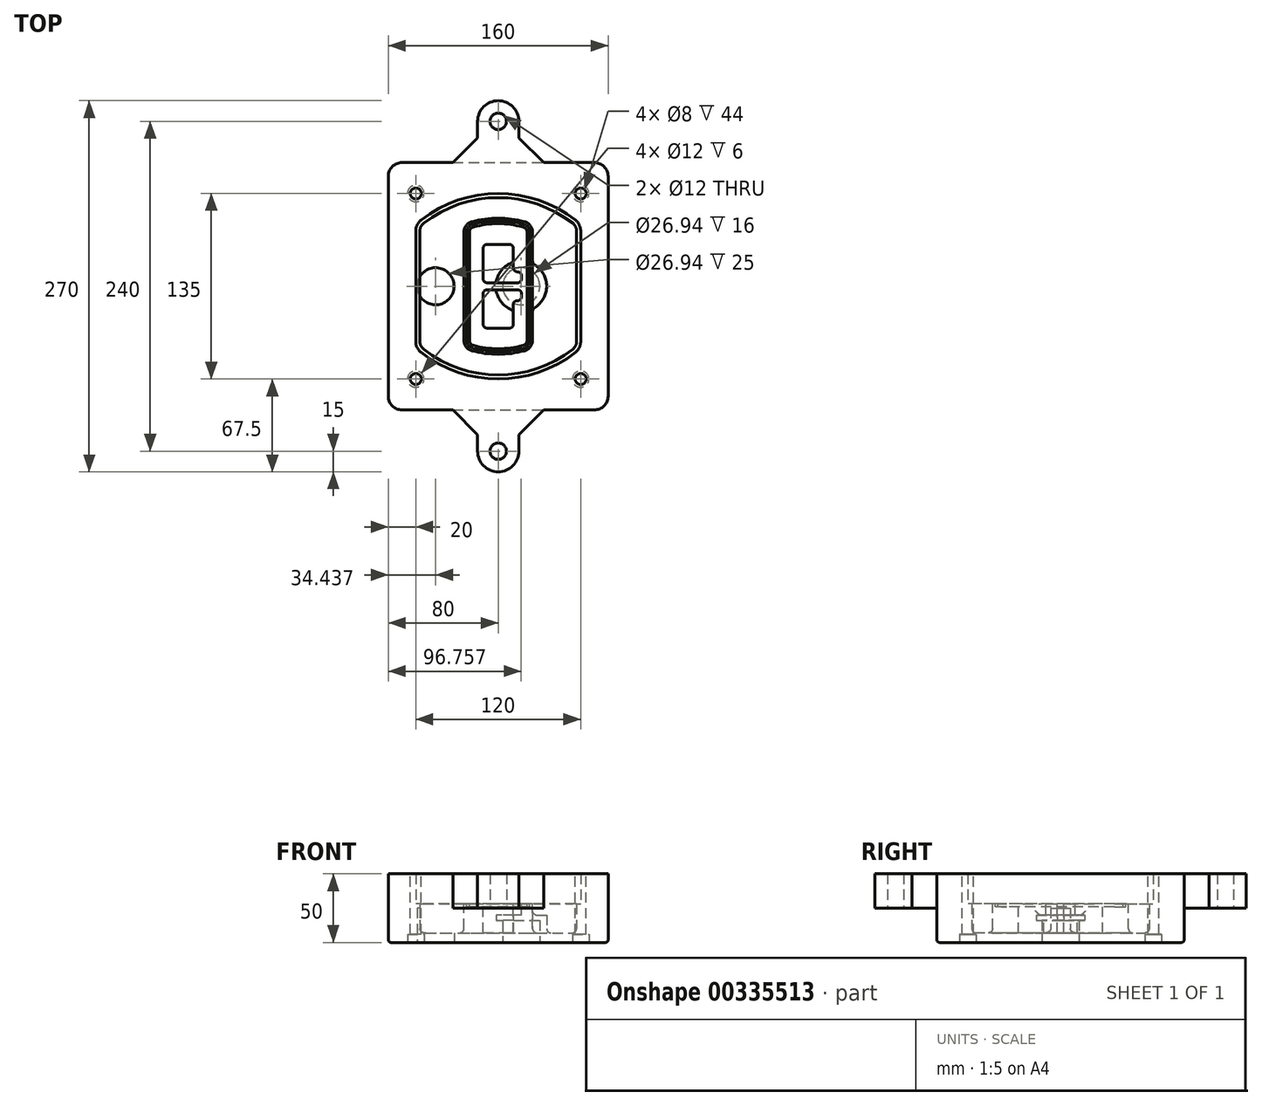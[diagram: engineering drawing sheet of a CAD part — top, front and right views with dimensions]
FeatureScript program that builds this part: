
annotation { "Feature Type Name" : "Feature", "Feature Type Description" : "" }
export const myFeature = defineFeature(function(context is Context, id is Id, definition is map)
    precondition{}
    {
        {
            var Q0;
            Q0=qCreatedBy(makeId("Top.planeOp"),FACE);
            var sketch = newSketch(context, id + "F0", { "sketchPlane" : qUnion([Q0])});
            skPoint(sketch, "E0.rect.middle", {"position": v(0, 0) * mm});
            skLineSegment(sketch, "E1.bottom", {"start": v(-70, -90) * mm, "end": v(70, -90) * mm});
            skLineSegment(sketch, "E1.top", {"start": v(-70, 90) * mm, "end": v(70, 90) * mm});
            skLineSegment(sketch, "E1.left", {"start": v(-80, -80) * mm, "end": v(-80, 80) * mm});
            skLineSegment(sketch, "E1.right", {"start": v(80, -80) * mm, "end": v(80, 80) * mm});
            skLineSegment(sketch, "E2", {"start": v(-80, 90) * mm, "end": v(80, -90) * mm, "construction": true});
            skLineSegment(sketch, "E3", {"start": v(80, 90) * mm, "end": v(-80, -90) * mm, "construction": true});
            skCircle(sketch, "E4", {"center": v(-60, 67.5) * mm, "radius": 4 * mm});
            skCircle(sketch, "E5", {"center": v(60, 67.5) * mm, "radius": 4 * mm});
            skCircle(sketch, "E6", {"center": v(60, -67.5) * mm, "radius": 4 * mm});
            skCircle(sketch, "E7", {"center": v(-60, -67.5) * mm, "radius": 4 * mm});
            skLineSegment(sketch, "E8", {"start": v(-60, 67.5) * mm, "end": v(60, 67.5) * mm, "construction": true});
            skLineSegment(sketch, "E9", {"start": v(60, 67.5) * mm, "end": v(60, -67.5) * mm, "construction": true});
            skLineSegment(sketch, "E10", {"start": v(60, -67.5) * mm, "end": v(-60, -67.5) * mm, "construction": true});
            skLineSegment(sketch, "E11", {"start": v(-60, -67.5) * mm, "end": v(-60, 67.5) * mm, "construction": true});
            skLineSegment(sketch, "E12", {"start": v(-60, 40.3) * mm, "end": v(-60, -40.3) * mm});
            skLineSegment(sketch, "E13", {"start": v(60, 40.3) * mm, "end": v(60, -40.3) * mm});
            skArc(sketch, "E14", {"start": v(56.15, 48.18) * mm, "mid": v(0, 67.5) * mm, "end": v(-56.15, 48.18) * mm});
            skArc(sketch, "E15", {"start": v(-56.15, -48.18) * mm, "mid": v(0, -67.5) * mm, "end": v(56.15, -48.18) * mm});
            skLineSegment(sketch, "E16", {"start": v(-60, 0) * mm, "end": v(60, 0) * mm, "construction": true});
            skPoint(sketch, "E17.visualSharp", {"position": v(-60, -45) * mm});
            skArc(sketch, "E17.filletArc", {"start": v(-60, -40.3) * mm, "mid": v(-58.99, -44.68) * mm, "end": v(-56.15, -48.18) * mm});
            skPoint(sketch, "E18.visualSharp", {"position": v(-60, 45) * mm});
            skArc(sketch, "E18.filletArc", {"start": v(-56.15, 48.18) * mm, "mid": v(-58.99, 44.68) * mm, "end": v(-60, 40.3) * mm});
            skPoint(sketch, "E19.visualSharp", {"position": v(60, 45) * mm});
            skArc(sketch, "E19.filletArc", {"start": v(60, 40.3) * mm, "mid": v(58.99, 44.68) * mm, "end": v(56.15, 48.18) * mm});
            skPoint(sketch, "E20.visualSharp", {"position": v(60, -45) * mm});
            skArc(sketch, "E20.filletArc", {"start": v(56.15, -48.18) * mm, "mid": v(58.99, -44.68) * mm, "end": v(60, -40.3) * mm});
            skPoint(sketch, "E21.visualSharp", {"position": v(-80, 90) * mm});
            skArc(sketch, "E21.filletArc", {"start": v(-70, 90) * mm, "mid": v(-77.07, 87.07) * mm, "end": v(-80, 80) * mm});
            skPoint(sketch, "E22.visualSharp", {"position": v(80, 90) * mm});
            skArc(sketch, "E22.filletArc", {"start": v(80, 80) * mm, "mid": v(77.07, 87.07) * mm, "end": v(70, 90) * mm});
            skPoint(sketch, "E23.visualSharp", {"position": v(80, -90) * mm});
            skArc(sketch, "E23.filletArc", {"start": v(70, -90) * mm, "mid": v(77.07, -87.07) * mm, "end": v(80, -80) * mm});
            skPoint(sketch, "E24.visualSharp", {"position": v(-80, -90) * mm});
            skArc(sketch, "E24.filletArc", {"start": v(-80, -80) * mm, "mid": v(-77.07, -87.07) * mm, "end": v(-70, -90) * mm});
            skArc(sketch, "E25.0", {"start": v(57, 40.3) * mm, "mid": v(56.3, 43.36) * mm, "end": v(54.3, 45.81) * mm});
            skLineSegment(sketch, "E25.1", {"start": v(57, 40.3) * mm, "end": v(57, -40.3) * mm});
            skArc(sketch, "E25.2", {"start": v(54.3, -45.81) * mm, "mid": v(56.3, -43.36) * mm, "end": v(57, -40.3) * mm});
            skArc(sketch, "E25.3", {"start": v(-54.3, -45.81) * mm, "mid": v(0, -64.5) * mm, "end": v(54.3, -45.81) * mm});
            skArc(sketch, "E25.4", {"start": v(-57, -40.3) * mm, "mid": v(-56.3, -43.36) * mm, "end": v(-54.3, -45.81) * mm});
            skArc(sketch, "E25.5", {"start": v(54.3, 45.81) * mm, "mid": v(0, 64.5) * mm, "end": v(-54.3, 45.81) * mm});
            skLineSegment(sketch, "E25.6", {"start": v(-57, 40.3) * mm, "end": v(-57, -40.3) * mm});
            skArc(sketch, "E25.7", {"start": v(-54.3, 45.81) * mm, "mid": v(-56.3, 43.36) * mm, "end": v(-57, 40.3) * mm});
            skArc(sketch, "E26.0", {"start": v(-58.62, 51.33) * mm, "mid": v(-62.58, 46.43) * mm, "end": v(-64, 40.3) * mm});
            skArc(sketch, "E26.1", {"start": v(58.62, 51.33) * mm, "mid": v(0, 71.5) * mm, "end": v(-58.62, 51.33) * mm});
            skArc(sketch, "E26.2", {"start": v(64, 40.3) * mm, "mid": v(62.58, 46.43) * mm, "end": v(58.62, 51.33) * mm});
            skLineSegment(sketch, "E26.3", {"start": v(64, 40.3) * mm, "end": v(64, -40.3) * mm});
            skArc(sketch, "E26.4", {"start": v(58.62, -51.33) * mm, "mid": v(62.58, -46.43) * mm, "end": v(64, -40.3) * mm});
            skLineSegment(sketch, "E26.5", {"start": v(-64, 40.3) * mm, "end": v(-64, -40.3) * mm});
            skArc(sketch, "E26.6", {"start": v(-58.62, -51.33) * mm, "mid": v(0, -71.5) * mm, "end": v(58.62, -51.33) * mm});
            skArc(sketch, "E26.7", {"start": v(-64, -40.3) * mm, "mid": v(-62.58, -46.43) * mm, "end": v(-58.62, -51.33) * mm});
            skSolve(sketch);
        }
        {
            var Q0;
            Q0=makeQuery(id+"F0.imprint","IMPRINT",FACE,{"disambiguationData":[TD([[makeQuery(id+"F0.imprint","IMPRINT",EDGE,{"derivedFrom":sQuery(id+"F0.wireOp",EDGE,"E1.bottom")}),1.0]])]});
            var Q1;
            Q1=makeQuery(id+"F0.imprint","IMPRINT",FACE,{"disambiguationData":[TD([[makeQuery(id+"F0.imprint","IMPRINT",EDGE,{"derivedFrom":sQuery(id+"F0.wireOp",EDGE,"E12")}),1.0]])]});
            var Q2;
            Q2=makeQuery(id+"F0.imprint","IMPRINT",FACE,{"disambiguationData":[TD([[makeQuery(id+"F0.imprint","IMPRINT",EDGE,{"derivedFrom":sQuery(id+"F0.wireOp",EDGE,"E25.0")}),1.0]])]});
            var Q3;
            Q3=makeQuery(id+"F0.imprint","IMPRINT",FACE,{"disambiguationData":[TD([[makeQuery(id+"F0.imprint","IMPRINT",EDGE,{"derivedFrom":sQuery(id+"F0.wireOp",EDGE,"E12")}),-1.0]])]});
            extrude(context, id + "F1", {"entities" : qUnion([Q0, Q1, Q2, Q3]), "oppositeDirection" : true, "depth" : 25 * mm});
        }
        {
            var Q0;
            Q0=makeQuery(id+"F0.imprint","IMPRINT",FACE,{"disambiguationData":[TD([[makeQuery(id+"F0.imprint","IMPRINT",EDGE,{"derivedFrom":sQuery(id+"F0.wireOp",EDGE,"E12")}),1.0]])]});
            extrude(context, id + "F2", {"entities" : qUnion([Q0]), "operationType" : NewBodyOperationType.ADD, "depth" : 3 * mm});
        }
        {
            var Q0;
            Q0=makeQuery(id+"F0.imprint","IMPRINT",FACE,{"disambiguationData":[TD([[makeQuery(id+"F0.imprint","IMPRINT",EDGE,{"derivedFrom":sQuery(id+"F0.wireOp",EDGE,"E25.0")}),1.0]])]});
            extrude(context, id + "F3", {"entities" : qUnion([Q0]), "operationType" : NewBodyOperationType.REMOVE, "oppositeDirection" : true, "depth" : 18 * mm});
        }
        {
            var Q0;
            Q0=makeQuery(id+"F2.opExtrude","CAP_FACE",FACE,{"disambiguationData":[OSD([sQuery(id+"F0.wireOp",EDGE,"E12"),sQuery(id+"F0.wireOp",EDGE,"E13"),sQuery(id+"F0.wireOp",EDGE,"E14"),sQuery(id+"F0.wireOp",EDGE,"E15"),sQuery(id+"F0.wireOp",EDGE,"E17.filletArc"),sQuery(id+"F0.wireOp",EDGE,"E18.filletArc"),sQuery(id+"F0.wireOp",EDGE,"E19.filletArc"),sQuery(id+"F0.wireOp",EDGE,"E20.filletArc"),sQuery(id+"F0.wireOp",EDGE,"E25.0"),sQuery(id+"F0.wireOp",EDGE,"E25.1"),sQuery(id+"F0.wireOp",EDGE,"E25.2"),sQuery(id+"F0.wireOp",EDGE,"E25.3"),sQuery(id+"F0.wireOp",EDGE,"E25.4"),sQuery(id+"F0.wireOp",EDGE,"E25.5"),sQuery(id+"F0.wireOp",EDGE,"E25.6"),sQuery(id+"F0.wireOp",EDGE,"E25.7")])],"isStart":false});
            var sketch = newSketch(context, id + "F4", { "sketchPlane" : qUnion([Q0])});
            skArc(sketch, "E27.0", {"start": v(-19.08, -46.97) * mm, "mid": v(0, -49.5) * mm, "end": v(19.08, -46.97) * mm});
            skArc(sketch, "E28.0", {"start": v(19.08, 46.97) * mm, "mid": v(0, 49.5) * mm, "end": v(-19.08, 46.97) * mm});
            skLineSegment(sketch, "E29", {"start": v(-25, 39.25) * mm, "end": v(-25, -39.25) * mm});
            skLineSegment(sketch, "E30", {"start": v(25, 39.25) * mm, "end": v(25, -39.25) * mm});
            skLineSegment(sketch, "E31", {"start": v(-25, 45.1) * mm, "end": v(25, 45.1) * mm, "construction": true});
            skLineSegment(sketch, "E32", {"start": v(-25, -45.1) * mm, "end": v(25, -45.1) * mm, "construction": true});
            skPoint(sketch, "E33.visualSharp", {"position": v(-25, 45.1) * mm});
            skArc(sketch, "E33.filletArc", {"start": v(-19.08, 46.97) * mm, "mid": v(-23.35, 44.11) * mm, "end": v(-25, 39.25) * mm});
            skPoint(sketch, "E34.visualSharp", {"position": v(25, 45.1) * mm});
            skArc(sketch, "E34.filletArc", {"start": v(25, 39.25) * mm, "mid": v(23.35, 44.11) * mm, "end": v(19.08, 46.97) * mm});
            skPoint(sketch, "E35.visualSharp", {"position": v(25, -45.1) * mm});
            skArc(sketch, "E35.filletArc", {"start": v(19.08, -46.97) * mm, "mid": v(23.35, -44.11) * mm, "end": v(25, -39.25) * mm});
            skPoint(sketch, "E36.visualSharp", {"position": v(-25, -45.1) * mm});
            skArc(sketch, "E36.filletArc", {"start": v(-25, -39.25) * mm, "mid": v(-23.35, -44.11) * mm, "end": v(-19.08, -46.97) * mm});
            skArc(sketch, "E37.0", {"start": v(54.3, 45.81) * mm, "mid": v(0, 64.5) * mm, "end": v(-54.3, 45.81) * mm});
            skArc(sketch, "E37.1", {"start": v(-54.3, 45.81) * mm, "mid": v(-56.3, 43.36) * mm, "end": v(-57, 40.3) * mm});
            skLineSegment(sketch, "E37.2", {"start": v(-57, 40.3) * mm, "end": v(-57, -40.3) * mm});
            skArc(sketch, "E37.3", {"start": v(-57, -40.3) * mm, "mid": v(-56.3, -43.36) * mm, "end": v(-54.3, -45.81) * mm});
            skArc(sketch, "E37.4", {"start": v(-54.3, -45.81) * mm, "mid": v(0, -64.5) * mm, "end": v(54.3, -45.81) * mm});
            skArc(sketch, "E37.5", {"start": v(54.3, -45.81) * mm, "mid": v(56.3, -43.36) * mm, "end": v(57, -40.3) * mm});
            skLineSegment(sketch, "E37.6", {"start": v(57, 40.3) * mm, "end": v(57, -40.3) * mm});
            skArc(sketch, "E37.7", {"start": v(57, 40.3) * mm, "mid": v(56.3, 43.36) * mm, "end": v(54.3, 45.81) * mm});
            skLineSegment(sketch, "E38.0", {"start": v(23, 39.25) * mm, "end": v(23, -39.25) * mm});
            skArc(sketch, "E38.1", {"start": v(18.56, -45.04) * mm, "mid": v(21.76, -42.9) * mm, "end": v(23, -39.25) * mm});
            skArc(sketch, "E38.2", {"start": v(-18.56, -45.04) * mm, "mid": v(0, -47.5) * mm, "end": v(18.56, -45.04) * mm});
            skArc(sketch, "E38.3", {"start": v(-23, -39.25) * mm, "mid": v(-21.76, -42.9) * mm, "end": v(-18.56, -45.04) * mm});
            skLineSegment(sketch, "E38.4", {"start": v(-23, 39.25) * mm, "end": v(-23, -39.25) * mm});
            skArc(sketch, "E38.5", {"start": v(23, 39.25) * mm, "mid": v(21.76, 42.9) * mm, "end": v(18.56, 45.04) * mm});
            skArc(sketch, "E38.6", {"start": v(-18.56, 45.04) * mm, "mid": v(-21.76, 42.9) * mm, "end": v(-23, 39.25) * mm});
            skArc(sketch, "E38.7", {"start": v(18.56, 45.04) * mm, "mid": v(0, 47.5) * mm, "end": v(-18.56, 45.04) * mm});
            skArc(sketch, "E39.0", {"start": v(21, 39.25) * mm, "mid": v(20.18, 41.68) * mm, "end": v(18.04, 43.1) * mm});
            skLineSegment(sketch, "E39.1", {"start": v(21, 39.25) * mm, "end": v(21, -39.25) * mm});
            skArc(sketch, "E39.2", {"start": v(18.04, -43.1) * mm, "mid": v(20.18, -41.68) * mm, "end": v(21, -39.25) * mm});
            skArc(sketch, "E39.3", {"start": v(-18.04, -43.1) * mm, "mid": v(0, -45.5) * mm, "end": v(18.04, -43.1) * mm});
            skArc(sketch, "E39.4", {"start": v(-21, -39.25) * mm, "mid": v(-20.18, -41.68) * mm, "end": v(-18.04, -43.1) * mm});
            skArc(sketch, "E39.5", {"start": v(18.04, 43.1) * mm, "mid": v(0, 45.5) * mm, "end": v(-18.04, 43.1) * mm});
            skLineSegment(sketch, "E39.6", {"start": v(-21, 39.25) * mm, "end": v(-21, -39.25) * mm});
            skArc(sketch, "E39.7", {"start": v(-18.04, 43.1) * mm, "mid": v(-20.18, 41.68) * mm, "end": v(-21, 39.25) * mm});
            skLineSegment(sketch, "E40", {"start": v(-25, 0) * mm, "end": v(25, 0) * mm, "construction": true});
            skLineSegment(sketch, "E41", {"start": v(-11, 5.5) * mm, "end": v(-11, 27.5) * mm});
            skLineSegment(sketch, "E42", {"start": v(-8, 30.5) * mm, "end": v(8, 30.5) * mm});
            skLineSegment(sketch, "E43", {"start": v(11, 27.5) * mm, "end": v(11, 13.5) * mm});
            skLineSegment(sketch, "E44", {"start": v(14, 10.5) * mm, "end": v(14, 10.5) * mm});
            skLineSegment(sketch, "E45", {"start": v(17, 7.5) * mm, "end": v(17, 5.5) * mm});
            skLineSegment(sketch, "E46", {"start": v(14, 2.5) * mm, "end": v(-8, 2.5) * mm});
            skPoint(sketch, "E47.visualSharp", {"position": v(-11, 30.5) * mm});
            skArc(sketch, "E47.filletArc", {"start": v(-8, 30.5) * mm, "mid": v(-10.12, 29.62) * mm, "end": v(-11, 27.5) * mm});
            skPoint(sketch, "E48.visualSharp", {"position": v(11, 30.5) * mm});
            skArc(sketch, "E48.filletArc", {"start": v(11, 27.5) * mm, "mid": v(10.12, 29.62) * mm, "end": v(8, 30.5) * mm});
            skPoint(sketch, "E49.visualSharp", {"position": v(11, 10.5) * mm});
            skArc(sketch, "E49.filletArc", {"start": v(11, 13.5) * mm, "mid": v(11.88, 11.38) * mm, "end": v(14, 10.5) * mm});
            skPoint(sketch, "E50.visualSharp", {"position": v(17, 10.5) * mm});
            skArc(sketch, "E50.filletArc", {"start": v(17, 7.5) * mm, "mid": v(16.12, 9.62) * mm, "end": v(14, 10.5) * mm});
            skPoint(sketch, "E51.visualSharp", {"position": v(17, 2.5) * mm});
            skArc(sketch, "E51.filletArc", {"start": v(14, 2.5) * mm, "mid": v(16.12, 3.38) * mm, "end": v(17, 5.5) * mm});
            skPoint(sketch, "E52.visualSharp", {"position": v(-11, 2.5) * mm});
            skArc(sketch, "E52.filletArc", {"start": v(-11, 5.5) * mm, "mid": v(-10.12, 3.38) * mm, "end": v(-8, 2.5) * mm});
            skLineSegment(sketch, "E53.0.MirrorCS", {"start": v(14, -2.5) * mm, "end": v(-8, -2.5) * mm});
            skArc(sketch, "E54.0.MirrorCS", {"start": v(-11, -5.5) * mm, "mid": v(-10.12, -3.38) * mm, "end": v(-8, -2.5) * mm});
            skLineSegment(sketch, "E55.0.MirrorCS", {"start": v(-11, -5.5) * mm, "end": v(-11, -27.5) * mm});
            skArc(sketch, "E56.0.MirrorCS", {"start": v(-8, -30.5) * mm, "mid": v(-10.12, -29.62) * mm, "end": v(-11, -27.5) * mm});
            skLineSegment(sketch, "E57.0.MirrorCS", {"start": v(-8, -30.5) * mm, "end": v(8, -30.5) * mm});
            skArc(sketch, "E58.0.MirrorCS", {"start": v(11, -27.5) * mm, "mid": v(10.12, -29.62) * mm, "end": v(8, -30.5) * mm});
            skLineSegment(sketch, "E59.0.MirrorCS", {"start": v(11, -27.5) * mm, "end": v(11, -13.5) * mm});
            skArc(sketch, "E60.0.MirrorCS", {"start": v(11, -13.5) * mm, "mid": v(11.88, -11.38) * mm, "end": v(14, -10.5) * mm});
            skArc(sketch, "E61.0.MirrorCS", {"start": v(17, -7.5) * mm, "mid": v(16.12, -9.62) * mm, "end": v(14, -10.5) * mm});
            skLineSegment(sketch, "E62.0.MirrorCS", {"start": v(17, -7.5) * mm, "end": v(17, -5.5) * mm});
            skArc(sketch, "E63.0.MirrorCS", {"start": v(14, -2.5) * mm, "mid": v(16.12, -3.38) * mm, "end": v(17, -5.5) * mm});
            skSolve(sketch);
        }
        {
            var Q0;
            Q0=makeQuery(id+"F4.imprint","IMPRINT",FACE,{"disambiguationData":[TD([[makeQuery(id+"F4.imprint","IMPRINT",EDGE,{"derivedFrom":sQuery(id+"F4.wireOp",EDGE,"E27.0")}),1.0]])]});
            var Q1;
            Q1=makeQuery(id+"F4.imprint","IMPRINT",FACE,{"disambiguationData":[TD([[makeQuery(id+"F4.imprint","IMPRINT",EDGE,{"derivedFrom":sQuery(id+"F4.wireOp",EDGE,"E38.0")}),-1.0]])]});
            var Q2;
            Q2=makeQuery(id+"F4.imprint","IMPRINT",FACE,{"disambiguationData":[TD([[makeQuery(id+"F4.imprint","IMPRINT",EDGE,{"derivedFrom":sQuery(id+"F4.wireOp",EDGE,"E39.0")}),1.0]])]});
            extrude(context, id + "F5", {"entities" : qUnion([Q0, Q1, Q2]), "operationType" : NewBodyOperationType.ADD, "endBound" : BoundingType.UP_TO_NEXT, "oppositeDirection" : true, "depth" : 25 * mm});
        }
        {
            var Q0;
            Q0=makeQuery(id+"F4.imprint","IMPRINT",FACE,{"disambiguationData":[TD([[makeQuery(id+"F4.imprint","IMPRINT",EDGE,{"derivedFrom":sQuery(id+"F4.wireOp",EDGE,"E38.0")}),-1.0]])]});
            extrude(context, id + "F6", {"entities" : qUnion([Q0]), "operationType" : NewBodyOperationType.REMOVE, "oppositeDirection" : true, "depth" : 2 * mm});
        }
        {
            var Q0;
            Q0=makeQuery(id+"F1.opExtrude","CAP_FACE",FACE,{"disambiguationData":[OSD([sQuery(id+"F0.wireOp",EDGE,"E1.bottom"),sQuery(id+"F0.wireOp",EDGE,"E1.top"),sQuery(id+"F0.wireOp",EDGE,"E1.left"),sQuery(id+"F0.wireOp",EDGE,"E1.right"),sQuery(id+"F0.wireOp",EDGE,"E4"),sQuery(id+"F0.wireOp",EDGE,"E5"),sQuery(id+"F0.wireOp",EDGE,"E6"),sQuery(id+"F0.wireOp",EDGE,"E7"),sQuery(id+"F0.wireOp",EDGE,"E21.filletArc"),sQuery(id+"F0.wireOp",EDGE,"E22.filletArc"),sQuery(id+"F0.wireOp",EDGE,"E23.filletArc"),sQuery(id+"F0.wireOp",EDGE,"E24.filletArc")])],"isStart":false});
            var sketch = newSketch(context, id + "F7", { "sketchPlane" : qUnion([Q0])});
            skCircle(sketch, "E64", {"center": v(16.76, 0) * mm, "radius": 13.47 * mm});
            skCircle(sketch, "E65", {"center": v(-45.56, 0) * mm, "radius": 13.47 * mm});
            skLineSegment(sketch, "E66", {"start": v(80, 0) * mm, "end": v(-80, 0) * mm});
            skCircle(sketch, "E67", {"center": v(16.76, 0) * mm, "radius": 18.47 * mm});
            skCircle(sketch, "E68", {"center": v(60, -67.5) * mm, "radius": 6 * mm});
            skCircle(sketch, "E69", {"center": v(-60, -67.5) * mm, "radius": 6 * mm});
            skCircle(sketch, "E70", {"center": v(-60, 67.5) * mm, "radius": 6 * mm});
            skCircle(sketch, "E71", {"center": v(60, 67.5) * mm, "radius": 6 * mm});
            skSolve(sketch);
        }
        {
            var Q0;
            {var subQ1=sQuery(id+"F7.wireOp",EDGE,"E66");var subQ4=sQuery(id+"F7.wireOp",EDGE,"E64");var subQ6=makeQuery(id+"F7.imprint","INTERSECT",VERTEX,{"disambiguationData":[OD(0.0)],"derivedFrom":[subQ4,subQ1]});Q0=makeQuery(id+"F7.imprint","IMPRINT",FACE,{"disambiguationData":[TD([[makeQuery(id+"F7.imprint","IMPRINT",EDGE,{"disambiguationData":[TD([[subQ6,-1.0]])],"derivedFrom":subQ4}),-1.0]])]});}
            var Q1;
            {var subQ0=sQuery(id+"F7.wireOp",EDGE,"E66");var subQ1=sQuery(id+"F7.wireOp",EDGE,"E64");var subQ3=makeQuery(id+"F7.imprint","INTERSECT",VERTEX,{"disambiguationData":[OD(0.0)],"derivedFrom":[subQ1,subQ0]});Q1=makeQuery(id+"F7.imprint","IMPRINT",FACE,{"disambiguationData":[TD([[makeQuery(id+"F7.imprint","IMPRINT",EDGE,{"disambiguationData":[TD([[subQ3,-1.0]])],"derivedFrom":subQ1}),1.0]])]});}
            var Q2;
            {var subQ0=sQuery(id+"F7.wireOp",EDGE,"E66");var subQ1=sQuery(id+"F7.wireOp",EDGE,"E64");var subQ3=makeQuery(id+"F7.imprint","INTERSECT",VERTEX,{"disambiguationData":[OD(0.0)],"derivedFrom":[subQ1,subQ0]});Q2=makeQuery(id+"F7.imprint","IMPRINT",FACE,{"disambiguationData":[TD([[makeQuery(id+"F7.imprint","IMPRINT",EDGE,{"disambiguationData":[TD([[subQ3,1.0]])],"derivedFrom":subQ1}),1.0]])]});}
            var Q3;
            {var subQ1=sQuery(id+"F7.wireOp",EDGE,"E66");var subQ4=sQuery(id+"F7.wireOp",EDGE,"E64");var subQ6=makeQuery(id+"F7.imprint","INTERSECT",VERTEX,{"disambiguationData":[OD(0.0)],"derivedFrom":[subQ4,subQ1]});Q3=makeQuery(id+"F7.imprint","IMPRINT",FACE,{"disambiguationData":[TD([[makeQuery(id+"F7.imprint","IMPRINT",EDGE,{"disambiguationData":[TD([[subQ6,1.0]])],"derivedFrom":subQ4}),-1.0]])]});}
            extrude(context, id + "F8", {"entities" : qUnion([Q0, Q1, Q2, Q3]), "operationType" : NewBodyOperationType.ADD, "oppositeDirection" : true, "depth" : 20 * mm});
        }
        {
            var Q0;
            {var subQ0=sQuery(id+"F7.wireOp",EDGE,"E66");var subQ1=sQuery(id+"F7.wireOp",EDGE,"E64");var subQ3=makeQuery(id+"F7.imprint","INTERSECT",VERTEX,{"disambiguationData":[OD(0.0)],"derivedFrom":[subQ1,subQ0]});Q0=makeQuery(id+"F7.imprint","IMPRINT",FACE,{"disambiguationData":[TD([[makeQuery(id+"F7.imprint","IMPRINT",EDGE,{"disambiguationData":[TD([[subQ3,-1.0]])],"derivedFrom":subQ1}),1.0]])]});}
            var Q1;
            {var subQ0=sQuery(id+"F7.wireOp",EDGE,"E66");var subQ1=sQuery(id+"F7.wireOp",EDGE,"E64");var subQ3=makeQuery(id+"F7.imprint","INTERSECT",VERTEX,{"disambiguationData":[OD(0.0)],"derivedFrom":[subQ1,subQ0]});Q1=makeQuery(id+"F7.imprint","IMPRINT",FACE,{"disambiguationData":[TD([[makeQuery(id+"F7.imprint","IMPRINT",EDGE,{"disambiguationData":[TD([[subQ3,1.0]])],"derivedFrom":subQ1}),1.0]])]});}
            extrude(context, id + "F9", {"entities" : qUnion([Q0, Q1]), "operationType" : NewBodyOperationType.REMOVE, "oppositeDirection" : true, "depth" : 16 * mm});
        }
        {
            var Q0;
            {var subQ0=sQuery(id+"F7.wireOp",EDGE,"E66");var subQ1=sQuery(id+"F7.wireOp",EDGE,"E65");var subQ3=makeQuery(id+"F7.imprint","INTERSECT",VERTEX,{"disambiguationData":[OD(0.0)],"derivedFrom":[subQ1,subQ0]});Q0=makeQuery(id+"F7.imprint","IMPRINT",FACE,{"disambiguationData":[TD([[makeQuery(id+"F7.imprint","IMPRINT",EDGE,{"disambiguationData":[TD([[subQ3,-1.0]])],"derivedFrom":subQ1}),1.0]])]});}
            var Q1;
            {var subQ0=sQuery(id+"F7.wireOp",EDGE,"E66");var subQ1=sQuery(id+"F7.wireOp",EDGE,"E65");var subQ3=makeQuery(id+"F7.imprint","INTERSECT",VERTEX,{"disambiguationData":[OD(0.0)],"derivedFrom":[subQ1,subQ0]});Q1=makeQuery(id+"F7.imprint","IMPRINT",FACE,{"disambiguationData":[TD([[makeQuery(id+"F7.imprint","IMPRINT",EDGE,{"disambiguationData":[TD([[subQ3,1.0]])],"derivedFrom":subQ1}),1.0]])]});}
            extrude(context, id + "F10", {"entities" : qUnion([Q0, Q1]), "operationType" : NewBodyOperationType.REMOVE, "oppositeDirection" : true, "depth" : 25 * mm});
        }
        {
            var Q0;
            Q0=makeQuery(id+"F7.imprint","IMPRINT",FACE,{"disambiguationData":[TD([[makeQuery(id+"F7.imprint","IMPRINT",EDGE,{"derivedFrom":sQuery(id+"F7.wireOp",EDGE,"E68")}),1.0]])]});
            var Q1;
            Q1=makeQuery(id+"F7.imprint","IMPRINT",FACE,{"disambiguationData":[TD([[makeQuery(id+"F7.imprint","IMPRINT",EDGE,{"derivedFrom":makeQuery(id+"F1.opExtrude","CAP_EDGE",EDGE,{"disambiguationData":[OSD([sQuery(id+"F0.wireOp",EDGE,"E5")])],"isStart":false})}),-1.0]])]});
            var Q2;
            Q2=makeQuery(id+"F7.imprint","IMPRINT",FACE,{"disambiguationData":[TD([[makeQuery(id+"F7.imprint","IMPRINT",EDGE,{"derivedFrom":sQuery(id+"F7.wireOp",EDGE,"E69")}),1.0]])]});
            var Q3;
            Q3=makeQuery(id+"F7.imprint","IMPRINT",FACE,{"disambiguationData":[TD([[makeQuery(id+"F7.imprint","IMPRINT",EDGE,{"derivedFrom":makeQuery(id+"F1.opExtrude","CAP_EDGE",EDGE,{"disambiguationData":[OSD([sQuery(id+"F0.wireOp",EDGE,"E4")])],"isStart":false})}),-1.0]])]});
            var Q4;
            Q4=makeQuery(id+"F7.imprint","IMPRINT",FACE,{"disambiguationData":[TD([[makeQuery(id+"F7.imprint","IMPRINT",EDGE,{"derivedFrom":sQuery(id+"F7.wireOp",EDGE,"E70")}),1.0]])]});
            var Q5;
            Q5=makeQuery(id+"F7.imprint","IMPRINT",FACE,{"disambiguationData":[TD([[makeQuery(id+"F7.imprint","IMPRINT",EDGE,{"derivedFrom":makeQuery(id+"F1.opExtrude","CAP_EDGE",EDGE,{"disambiguationData":[OSD([sQuery(id+"F0.wireOp",EDGE,"E7")])],"isStart":false})}),-1.0]])]});
            var Q6;
            Q6=makeQuery(id+"F7.imprint","IMPRINT",FACE,{"disambiguationData":[TD([[makeQuery(id+"F7.imprint","IMPRINT",EDGE,{"derivedFrom":sQuery(id+"F7.wireOp",EDGE,"E71")}),1.0]])]});
            var Q7;
            Q7=makeQuery(id+"F7.imprint","IMPRINT",FACE,{"disambiguationData":[TD([[makeQuery(id+"F7.imprint","IMPRINT",EDGE,{"derivedFrom":makeQuery(id+"F1.opExtrude","CAP_EDGE",EDGE,{"disambiguationData":[OSD([sQuery(id+"F0.wireOp",EDGE,"E6")])],"isStart":false})}),-1.0]])]});
            extrude(context, id + "F11", {"entities" : qUnion([Q0, Q1, Q2, Q3, Q4, Q5, Q6, Q7]), "operationType" : NewBodyOperationType.REMOVE, "oppositeDirection" : true, "depth" : 6 * mm});
        }
        {
            var Q0;
            Q0=makeQuery(id+"F9.boolean.opBoolean","COPY",FACE,{"derivedFrom":makeQuery(id+"F9.opExtrude","CAP_FACE",FACE,{"disambiguationData":[OSD([sQuery(id+"F7.wireOp",EDGE,"E64")])],"isStart":false})});
            var sketch = newSketch(context, id + "F12", { "sketchPlane" : qUnion([Q0])});
            skArc(sketch, "E72.0", {"start": v(11, 17.55) * mm, "mid": v(2.57, 11.82) * mm, "end": v(-1.54, 2.5) * mm});
            skArc(sketch, "E72.1", {"start": v(-1.54, -2.5) * mm, "mid": v(2.57, -11.82) * mm, "end": v(11, -17.55) * mm});
            skLineSegment(sketch, "E73", {"start": v(-1.54, -2.5) * mm, "end": v(14, -2.5) * mm});
            skLineSegment(sketch, "E74.0", {"start": v(14, 2.5) * mm, "end": v(-1.54, 2.5) * mm});
            skArc(sketch, "E74.1", {"start": v(14, 2.5) * mm, "mid": v(16.12, 3.38) * mm, "end": v(17, 5.5) * mm});
            skLineSegment(sketch, "E74.2", {"start": v(17, 7.5) * mm, "end": v(17, 5.5) * mm});
            skArc(sketch, "E74.3", {"start": v(17, 7.5) * mm, "mid": v(16.12, 9.62) * mm, "end": v(14, 10.5) * mm});
            skArc(sketch, "E74.4", {"start": v(11, 13.5) * mm, "mid": v(11.88, 11.38) * mm, "end": v(14, 10.5) * mm});
            skLineSegment(sketch, "E74.5", {"start": v(11, 17.55) * mm, "end": v(11, 13.5) * mm});
            skLineSegment(sketch, "E74.7", {"start": v(14, -2.5) * mm, "end": v(-1.54, -2.5) * mm});
            skArc(sketch, "E74.8", {"start": v(14, -2.5) * mm, "mid": v(16.12, -3.38) * mm, "end": v(17, -5.5) * mm});
            skLineSegment(sketch, "E74.9", {"start": v(17, -7.5) * mm, "end": v(17, -5.5) * mm});
            skArc(sketch, "E74.10", {"start": v(17, -7.5) * mm, "mid": v(16.12, -9.62) * mm, "end": v(14, -10.5) * mm});
            skArc(sketch, "E74.11", {"start": v(11, -13.5) * mm, "mid": v(11.88, -11.38) * mm, "end": v(14, -10.5) * mm});
            skLineSegment(sketch, "E74.12", {"start": v(11, -17.55) * mm, "end": v(11, -13.5) * mm});
            skPoint(sketch, "E75.orphan", {"position": v(11, -27.5) * mm});
            skPoint(sketch, "E76.orphan", {"position": v(-8, -2.5) * mm});
            skPoint(sketch, "E77.orphan", {"position": v(-8, 2.5) * mm});
            skPoint(sketch, "E78.orphan", {"position": v(11, 27.5) * mm});
            skSolve(sketch);
        }
        {
            var Q0;
            {var subQ7=sQuery(id+"F12.wireOp",EDGE,"E72.0");var subQ14=sQuery(id+"F12.wireOp",EDGE,"E72.1");var subQ16=sQuery(id+"F12.wireOp",EDGE,"E74.1");var subQ18=sQuery(id+"F12.wireOp",EDGE,"E74.8");Q0=qUnion([makeQuery(id+"F12.imprint","IMPRINT",FACE,{"disambiguationData":[TD([[makeQuery(id+"F12.imprint","IMPRINT",EDGE,{"derivedFrom":subQ7}),1.0]])]}),makeQuery(id+"F12.imprint","IMPRINT",FACE,{"disambiguationData":[TD([[makeQuery(id+"F12.imprint","IMPRINT",EDGE,{"derivedFrom":subQ14}),1.0]])]}),makeQuery(id+"F12.imprint","IMPRINT",FACE,{"disambiguationData":[TD([[makeQuery(id+"F12.imprint","IMPRINT",EDGE,{"derivedFrom":subQ16}),1.0]])]}),makeQuery(id+"F12.imprint","IMPRINT",FACE,{"disambiguationData":[TD([[makeQuery(id+"F12.imprint","IMPRINT",EDGE,{"derivedFrom":subQ18}),-1.0]])]})]);}
            var Q1;
            Q1=makeQuery(id+"F5.boolean.opBoolean","SPLIT",FACE,{"disambiguationData":[TD([makeQuery(id+"F5.opExtrude","SWEPT_FACE",FACE,{"disambiguationData":[OSD([sQuery(id+"F4.wireOp",EDGE,"E41")])]})])],"derivedFrom":makeQuery(id+"F3.boolean.opBoolean","COPY",FACE,{"derivedFrom":makeQuery(id+"F3.opExtrude","CAP_FACE",FACE,{"disambiguationData":[OSD([sQuery(id+"F0.wireOp",EDGE,"E25.0"),sQuery(id+"F0.wireOp",EDGE,"E25.1"),sQuery(id+"F0.wireOp",EDGE,"E25.2"),sQuery(id+"F0.wireOp",EDGE,"E25.3"),sQuery(id+"F0.wireOp",EDGE,"E25.4"),sQuery(id+"F0.wireOp",EDGE,"E25.5"),sQuery(id+"F0.wireOp",EDGE,"E25.6"),sQuery(id+"F0.wireOp",EDGE,"E25.7")])],"isStart":false})})});
            extrude(context, id + "F13", {"entities" : qUnion([Q0]), "operationType" : NewBodyOperationType.REMOVE, "endBound" : BoundingType.UP_TO_SURFACE, "endBoundEntityFace" : qUnion([Q1]), "depth" : 25 * mm});
        }
        {
            var Q0;
            Q0=makeQuery(id+"F3.boolean.opBoolean","COPY",EDGE,{"derivedFrom":makeQuery(id+"F3.opExtrude","CAP_EDGE",EDGE,{"disambiguationData":[OSD([sQuery(id+"F0.wireOp",EDGE,"E25.6")])],"isStart":false})});
            var Q1;
            Q1=makeQuery(id+"F8.boolean.opBoolean","INTERSECT",EDGE,{"derivedFrom":[makeQuery(id+"F5.opExtrude","SWEPT_FACE",FACE,{"disambiguationData":[OSD([sQuery(id+"F4.wireOp",EDGE,"E30")])]}),makeQuery(id+"F8.opExtrude","CAP_FACE",FACE,{"disambiguationData":[OSD([sQuery(id+"F7.wireOp",EDGE,"E67")])],"isStart":false})]});
            var Q2;
            Q2=makeQuery(id+"F8.boolean.opBoolean","INTERSECT",EDGE,{"disambiguationData":[OD(1.0)],"derivedFrom":[makeQuery(id+"F5.opExtrude","SWEPT_FACE",FACE,{"disambiguationData":[OSD([sQuery(id+"F4.wireOp",EDGE,"E30")])]}),makeQuery(id+"F8.opExtrude","SWEPT_FACE",FACE,{"disambiguationData":[OSD([sQuery(id+"F7.wireOp",EDGE,"E67")])]})]});
            var Q3;
            {var subQ0=sQuery(id+"F4.wireOp",EDGE,"E30");Q3=makeQuery(id+"F8.boolean.opBoolean","SPLIT",EDGE,{"disambiguationData":[TD([makeQuery(id+"F5.opExtrude","SWEPT_FACE",FACE,{"disambiguationData":[OSD([sQuery(id+"F4.wireOp",EDGE,"E35.filletArc")])]})])],"derivedFrom":makeQuery(id+"F5.opExtrude","CAP_EDGE",EDGE,{"disambiguationData":[OSD([subQ0])],"isStart":false})});}
            var Q4;
            {var subQ0=sQuery(id+"F0.wireOp",EDGE,"E25.7");var subQ1=sQuery(id+"F0.wireOp",EDGE,"E25.1");var subQ2=sQuery(id+"F0.wireOp",EDGE,"E25.6");var subQ3=sQuery(id+"F0.wireOp",EDGE,"E25.5");var subQ4=sQuery(id+"F0.wireOp",EDGE,"E25.4");var subQ5=sQuery(id+"F0.wireOp",EDGE,"E25.0");var subQ6=sQuery(id+"F0.wireOp",EDGE,"E25.2");var subQ7=sQuery(id+"F0.wireOp",EDGE,"E25.3");Q4=makeQuery(id+"F8.boolean.opBoolean","INTERSECT",EDGE,{"derivedFrom":[makeQuery(id+"F5.boolean.opBoolean","SPLIT",FACE,{"disambiguationData":[TD([makeQuery(id+"F2.opExtrude","SWEPT_FACE",FACE,{"disambiguationData":[OSD([subQ5])]})])],"derivedFrom":makeQuery(id+"F3.boolean.opBoolean","COPY",FACE,{"derivedFrom":makeQuery(id+"F3.opExtrude","CAP_FACE",FACE,{"disambiguationData":[OSD([subQ5,subQ1,subQ6,subQ7,subQ4,subQ3,subQ2,subQ0])],"isStart":false})})}),makeQuery(id+"F8.opExtrude","SWEPT_FACE",FACE,{"disambiguationData":[OSD([sQuery(id+"F7.wireOp",EDGE,"E67")])]})]});}
            var Q5;
            Q5=makeQuery(id+"F8.boolean.opBoolean","INTERSECT",EDGE,{"disambiguationData":[OD(0.0)],"derivedFrom":[makeQuery(id+"F5.opExtrude","SWEPT_FACE",FACE,{"disambiguationData":[OSD([sQuery(id+"F4.wireOp",EDGE,"E30")])]}),makeQuery(id+"F8.opExtrude","SWEPT_FACE",FACE,{"disambiguationData":[OSD([sQuery(id+"F7.wireOp",EDGE,"E67")])]})]});
            fillet(context, id + "F14", {"entities" : qUnion([Q0, Q1, Q2, Q3, Q4, Q5]), "radius" : 3 * mm, "tangentPropagation" : true, "allowEdgeOverflow" : false});
        }
        {
            var Q0;
            Q0=makeQuery(id+"F1.opExtrude","CAP_EDGE",EDGE,{"disambiguationData":[OSD([sQuery(id+"F0.wireOp",EDGE,"E1.bottom")])],"isStart":false});
            fillet(context, id + "F15", {"entities" : qUnion([Q0]), "radius" : 2 * mm, "tangentPropagation" : true, "allowEdgeOverflow" : false});
        }
        {
            var Q0;
            {var subQ0=sQuery(id+"F0.wireOp",EDGE,"E21.filletArc");var subQ1=sQuery(id+"F0.wireOp",EDGE,"E7");var subQ2=sQuery(id+"F0.wireOp",EDGE,"E6");var subQ3=sQuery(id+"F0.wireOp",EDGE,"E5");var subQ4=sQuery(id+"F0.wireOp",EDGE,"E4");var subQ5=sQuery(id+"F0.wireOp",EDGE,"E22.filletArc");var subQ6=sQuery(id+"F0.wireOp",EDGE,"E1.bottom");var subQ7=sQuery(id+"F0.wireOp",EDGE,"E1.right");var subQ8=sQuery(id+"F0.wireOp",EDGE,"E1.top");var subQ9=sQuery(id+"F0.wireOp",EDGE,"E1.left");var subQ10=sQuery(id+"F0.wireOp",EDGE,"E23.filletArc");var subQ11=sQuery(id+"F0.wireOp",EDGE,"E24.filletArc");Q0=makeQuery(id+"F2.boolean.opBoolean","SPLIT",FACE,{"disambiguationData":[TD([makeQuery(id+"F1.opExtrude","SWEPT_FACE",FACE,{"disambiguationData":[OSD([subQ6])]})])],"derivedFrom":makeQuery(id+"F1.opExtrude","CAP_FACE",FACE,{"disambiguationData":[OSD([subQ6,subQ8,subQ9,subQ7,subQ4,subQ3,subQ2,subQ1,subQ0,subQ5,subQ10,subQ11])],"isStart":true})});}
            var sketch = newSketch(context, id + "F16", { "sketchPlane" : qUnion([Q0])});
            skLineSegment(sketch, "E79.0", {"start": v(-70, 90) * mm, "end": v(70, 90) * mm});
            skLineSegment(sketch, "E79.1", {"start": v(-80, -80) * mm, "end": v(-80, 80) * mm});
            skLineSegment(sketch, "E79.2", {"start": v(-70, -90) * mm, "end": v(70, -90) * mm});
            skLineSegment(sketch, "E79.3", {"start": v(80, -80) * mm, "end": v(80, 80) * mm});
            skArc(sketch, "E79.4", {"start": v(80, 80) * mm, "mid": v(77.07, 87.07) * mm, "end": v(70, 90) * mm});
            skArc(sketch, "E79.5", {"start": v(-70, 90) * mm, "mid": v(-77.07, 87.07) * mm, "end": v(-80, 80) * mm});
            skArc(sketch, "E79.6", {"start": v(-80, -80) * mm, "mid": v(-77.07, -87.07) * mm, "end": v(-70, -90) * mm});
            skArc(sketch, "E79.7", {"start": v(70, -90) * mm, "mid": v(77.07, -87.07) * mm, "end": v(80, -80) * mm});
            skCircle(sketch, "E79.8", {"center": v(60, -67.5) * mm, "radius": 4 * mm});
            skCircle(sketch, "E79.9", {"center": v(-60, -67.5) * mm, "radius": 4 * mm});
            skLineSegment(sketch, "E79.10", {"start": v(-60, 40.3) * mm, "end": v(-60, -40.3) * mm});
            skArc(sketch, "E79.11", {"start": v(56.15, 48.18) * mm, "mid": v(0, 67.5) * mm, "end": v(-56.15, 48.18) * mm});
            skArc(sketch, "E79.12", {"start": v(-56.15, 48.18) * mm, "mid": v(-58.99, 44.68) * mm, "end": v(-60, 40.3) * mm});
            skArc(sketch, "E79.13", {"start": v(60, 40.3) * mm, "mid": v(58.99, 44.68) * mm, "end": v(56.15, 48.18) * mm});
            skLineSegment(sketch, "E79.14", {"start": v(60, 40.3) * mm, "end": v(60, -40.3) * mm});
            skArc(sketch, "E79.15", {"start": v(-56.15, -48.18) * mm, "mid": v(0, -67.5) * mm, "end": v(56.15, -48.18) * mm});
            skArc(sketch, "E79.16", {"start": v(-60, -40.3) * mm, "mid": v(-58.99, -44.68) * mm, "end": v(-56.15, -48.18) * mm});
            skArc(sketch, "E79.17", {"start": v(56.15, -48.18) * mm, "mid": v(58.99, -44.68) * mm, "end": v(60, -40.3) * mm});
            skCircle(sketch, "E79.18", {"center": v(-60, 67.5) * mm, "radius": 4 * mm});
            skCircle(sketch, "E79.19", {"center": v(60, 67.5) * mm, "radius": 4 * mm});
            skLineSegment(sketch, "E80", {"start": v(-15, 108) * mm, "end": v(-15, 120) * mm});
            skLineSegment(sketch, "E81", {"start": v(33, 90) * mm, "end": v(15, 108) * mm});
            skLineSegment(sketch, "E82", {"start": v(15, 108) * mm, "end": v(15, 120) * mm});
            skArc(sketch, "E83", {"start": v(15, 120) * mm, "mid": v(0, 135) * mm, "end": v(-15, 120) * mm});
            skCircle(sketch, "E84", {"center": v(0, 120) * mm, "radius": 6 * mm});
            skLineSegment(sketch, "E85", {"start": v(-15, 108) * mm, "end": v(-33, 90) * mm});
            skLineSegment(sketch, "E86", {"start": v(0, 120) * mm, "end": v(0, 90) * mm, "construction": true});
            skLineSegment(sketch, "E87", {"start": v(0, 0) * mm, "end": v(-80, 0) * mm, "construction": true});
            skLineSegment(sketch, "E88", {"start": v(0, 0) * mm, "end": v(80, 0) * mm, "construction": true});
            skLineSegment(sketch, "E89.MirrorCS", {"start": v(-15, -108) * mm, "end": v(-15, -120) * mm});
            skLineSegment(sketch, "E90.MirrorCS", {"start": v(33, -90) * mm, "end": v(15, -108) * mm});
            skLineSegment(sketch, "E91.MirrorCS", {"start": v(15, -108) * mm, "end": v(15, -120) * mm});
            skArc(sketch, "E92.MirrorCS", {"start": v(15, -120) * mm, "mid": v(0, -135) * mm, "end": v(-15, -120) * mm});
            skLineSegment(sketch, "E93.MirrorCS", {"start": v(-15, -108) * mm, "end": v(-33, -90) * mm});
            skLineSegment(sketch, "E94.MirrorCS", {"start": v(0, -120) * mm, "end": v(0, -90) * mm, "construction": true});
            skCircle(sketch, "E95.MirrorC", {"center": v(0, -120) * mm, "radius": 6 * mm});
            skSolve(sketch);
        }
        {
            var Q0;
            Q0=makeQuery(id+"F16.imprint","IMPRINT",FACE,{"disambiguationData":[TD([[makeQuery(id+"F16.imprint","IMPRINT",EDGE,{"derivedFrom":sQuery(id+"F16.wireOp",EDGE,"E79.1")}),-1.0]])]});
            var Q1;
            Q1=makeQuery(id+"F16.imprint","IMPRINT",FACE,{"disambiguationData":[TD([[makeQuery(id+"F16.imprint","IMPRINT",EDGE,{"derivedFrom":sQuery(id+"F16.wireOp",EDGE,"E80")}),-1.0]])]});
            var Q2;
            Q2=makeQuery(id+"F16.imprint","IMPRINT",FACE,{"disambiguationData":[TD([[makeQuery(id+"F16.imprint","IMPRINT",EDGE,{"derivedFrom":sQuery(id+"F16.wireOp",EDGE,"E89.MirrorCS")}),1.0]])]});
            extrude(context, id + "F17", {"entities" : qUnion([Q0, Q1, Q2]), "operationType" : NewBodyOperationType.ADD, "depth" : 25 * mm});
        }
    });
